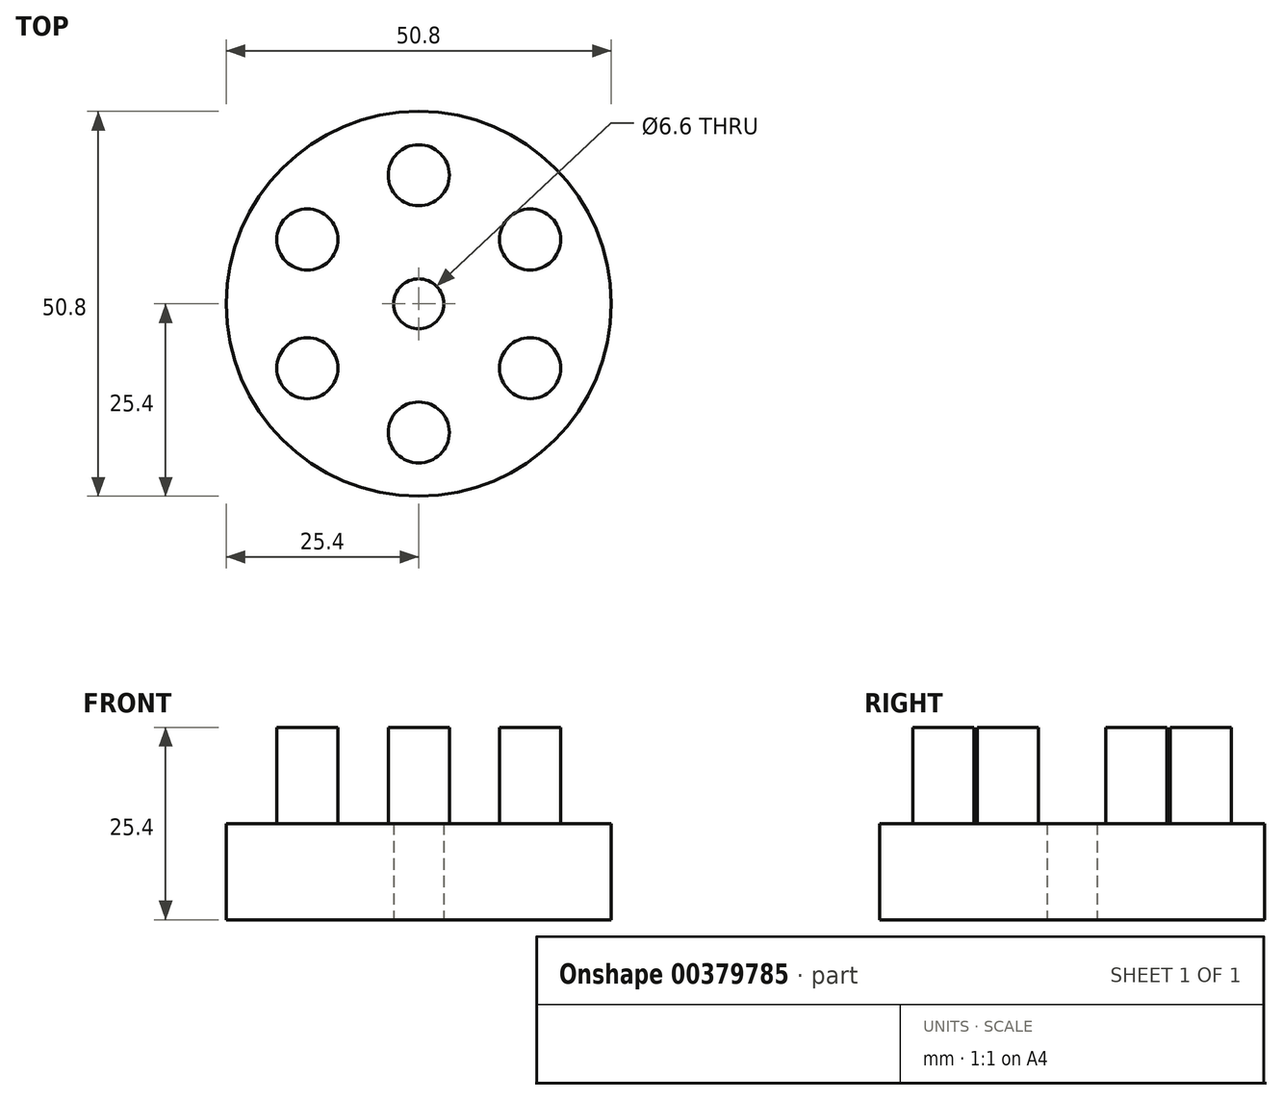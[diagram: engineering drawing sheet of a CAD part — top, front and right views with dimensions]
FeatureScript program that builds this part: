
annotation { "Feature Type Name" : "Feature", "Feature Type Description" : "" }
export const myFeature = defineFeature(function(context is Context, id is Id, definition is map)
    precondition{}
    {
        {
            var Q0;
            Q0=qCreatedBy(makeId("Top.planeOp"),FACE);
            var sketch = newSketch(context, id + "F0", { "sketchPlane" : qUnion([Q0])});
            skCircle(sketch, "E0", {"center": v(0, 0) * mm, "radius": 25.4 * mm});
            skCircle(sketch, "E1", {"center": v(0, 0) * mm, "radius": 3.3 * mm});
            skCircle(sketch, "E2", {"center": v(0, 19) * mm, "radius": 2.83 * mm});
            skCircle(sketch, "E3.1.0", {"center": v(-13.43, 13.43) * mm, "radius": 2.83 * mm});
            skCircle(sketch, "E3.2.0", {"center": v(-19, 0) * mm, "radius": 2.83 * mm});
            skCircle(sketch, "E3.3.0", {"center": v(-13.43, -13.43) * mm, "radius": 2.83 * mm});
            skCircle(sketch, "E3.4.0", {"center": v(0, -19) * mm, "radius": 2.83 * mm});
            skCircle(sketch, "E3.5.0", {"center": v(13.43, -13.43) * mm, "radius": 2.83 * mm});
            skCircle(sketch, "E3.6.0", {"center": v(19, 0) * mm, "radius": 2.83 * mm});
            skCircle(sketch, "E3.7.0", {"center": v(13.43, 13.43) * mm, "radius": 2.83 * mm});
            skSolve(sketch);
        }
        {
            var Q0;
            Q0=makeQuery(id+"F0.imprint","IMPRINT",FACE,{"disambiguationData":[TD([[makeQuery(id+"F0.imprint","IMPRINT",EDGE,{"derivedFrom":sQuery(id+"F0.wireOp",EDGE,"E3.2.0")}),1.0]])]});
            var Q1;
            Q1=makeQuery(id+"F0.imprint","IMPRINT",FACE,{"disambiguationData":[TD([[makeQuery(id+"F0.imprint","IMPRINT",EDGE,{"derivedFrom":sQuery(id+"F0.wireOp",EDGE,"E3.1.0")}),1.0]])]});
            var Q2;
            Q2=makeQuery(id+"F0.imprint","IMPRINT",FACE,{"disambiguationData":[TD([[makeQuery(id+"F0.imprint","IMPRINT",EDGE,{"derivedFrom":sQuery(id+"F0.wireOp",EDGE,"E2")}),1.0]])]});
            var Q3;
            Q3=makeQuery(id+"F0.imprint","IMPRINT",FACE,{"disambiguationData":[TD([[makeQuery(id+"F0.imprint","IMPRINT",EDGE,{"derivedFrom":sQuery(id+"F0.wireOp",EDGE,"E3.7.0")}),1.0]])]});
            var Q4;
            Q4=makeQuery(id+"F0.imprint","IMPRINT",FACE,{"disambiguationData":[TD([[makeQuery(id+"F0.imprint","IMPRINT",EDGE,{"derivedFrom":sQuery(id+"F0.wireOp",EDGE,"E3.6.0")}),1.0]])]});
            var Q5;
            Q5=makeQuery(id+"F0.imprint","IMPRINT",FACE,{"disambiguationData":[TD([[makeQuery(id+"F0.imprint","IMPRINT",EDGE,{"derivedFrom":sQuery(id+"F0.wireOp",EDGE,"E3.4.0")}),1.0]])]});
            var Q6;
            Q6=makeQuery(id+"F0.imprint","IMPRINT",FACE,{"disambiguationData":[TD([[makeQuery(id+"F0.imprint","IMPRINT",EDGE,{"derivedFrom":sQuery(id+"F0.wireOp",EDGE,"E3.5.0")}),1.0]])]});
            var Q7;
            Q7=makeQuery(id+"F0.imprint","IMPRINT",FACE,{"disambiguationData":[TD([[makeQuery(id+"F0.imprint","IMPRINT",EDGE,{"derivedFrom":sQuery(id+"F0.wireOp",EDGE,"E3.3.0")}),1.0]])]});
            var Q8;
            Q8=makeQuery(id+"F0.imprint","IMPRINT",FACE,{"disambiguationData":[TD([[makeQuery(id+"F0.imprint","IMPRINT",EDGE,{"derivedFrom":sQuery(id+"F0.wireOp",EDGE,"E0")}),1.0]])]});
            extrude(context, id + "F1", {"entities" : qUnion([Q0, Q1, Q2, Q3, Q4, Q5, Q6, Q7, Q8]), "depth" : 6.35 * mm});
        }
        {
            var Q0;
            Q0=makeQuery(id+"F1.opExtrude","CAP_FACE",FACE,{"disambiguationData":[OSD([sQuery(id+"F0.wireOp",EDGE,"E0"),sQuery(id+"F0.wireOp",EDGE,"E1"),sQuery(id+"F0.wireOp",EDGE,"E2"),sQuery(id+"F0.wireOp",EDGE,"E3.1.0"),sQuery(id+"F0.wireOp",EDGE,"E3.2.0"),sQuery(id+"F0.wireOp",EDGE,"E3.3.0"),sQuery(id+"F0.wireOp",EDGE,"E3.4.0"),sQuery(id+"F0.wireOp",EDGE,"E3.5.0"),sQuery(id+"F0.wireOp",EDGE,"E3.6.0"),sQuery(id+"F0.wireOp",EDGE,"E3.7.0")])],"isStart":false});
            extrude(context, id + "F2", {"entities" : qUnion([Q0]), "operationType" : NewBodyOperationType.ADD, "depth" : 6.35 * mm});
        }
        {
            var Q0;
            Q0=makeQuery(id+"F2.opExtrude","CAP_FACE",FACE,{"disambiguationData":[OSD([sQuery(id+"F0.wireOp",EDGE,"E0"),sQuery(id+"F0.wireOp",EDGE,"E1")])],"isStart":false});
            var sketch = newSketch(context, id + "F3", { "sketchPlane" : qUnion([Q0])});
            skCircle(sketch, "E4", {"center": v(0, 16.98) * mm, "radius": 4.03 * mm});
            skCircle(sketch, "E5.1.0", {"center": v(-14.7, 8.5) * mm, "radius": 4.03 * mm});
            skCircle(sketch, "E5.2.0", {"center": v(-14.7, -8.5) * mm, "radius": 4.03 * mm});
            skCircle(sketch, "E5.3.0", {"center": v(0, -16.98) * mm, "radius": 4.03 * mm});
            skCircle(sketch, "E5.4.0", {"center": v(14.7, -8.5) * mm, "radius": 4.03 * mm});
            skCircle(sketch, "E5.5.0", {"center": v(14.7, 8.5) * mm, "radius": 4.03 * mm});
            skPoint(sketch, "E5.center", {"position": v(0, 0) * mm});
            skSolve(sketch);
        }
        {
            var Q0;
            Q0 = qSketchRegion(id + "F3", true);
            extrude(context, id + "F4", {"entities" : qUnion([Q0]), "operationType" : NewBodyOperationType.ADD, "depth" : 12.7 * mm});
        }
    });
